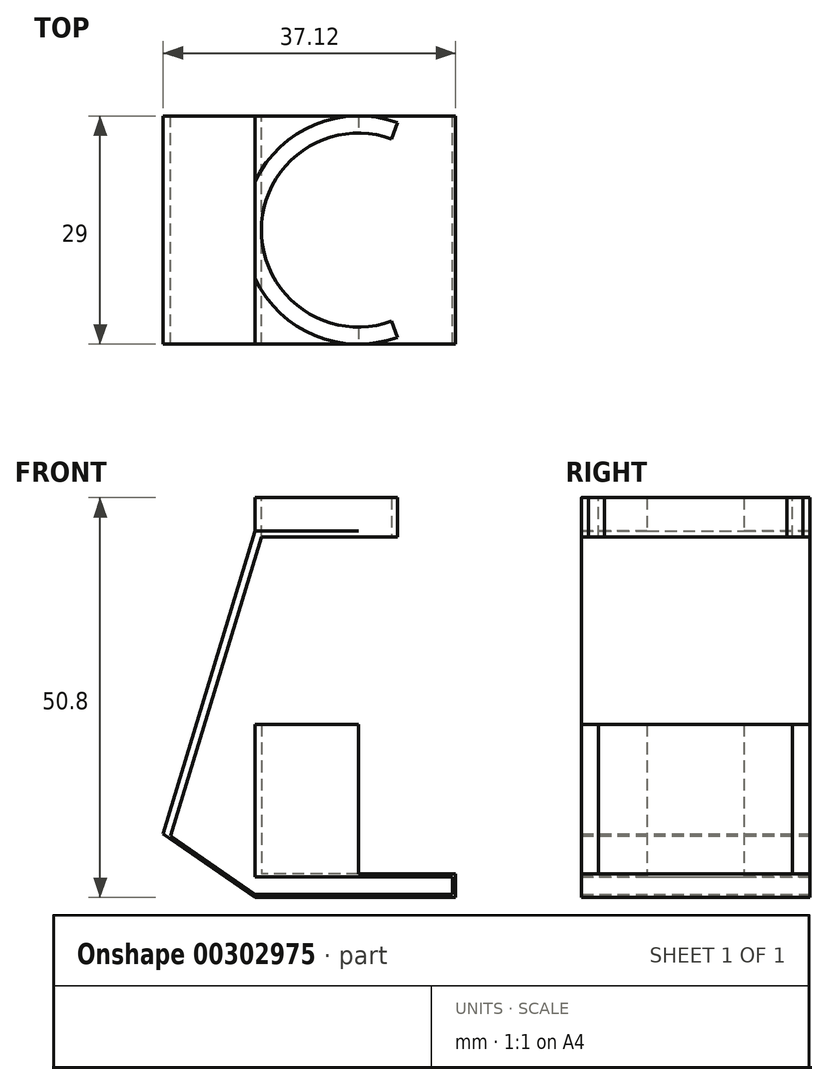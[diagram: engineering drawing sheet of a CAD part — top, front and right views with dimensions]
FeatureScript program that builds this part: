
annotation { "Feature Type Name" : "Feature", "Feature Type Description" : "" }
export const myFeature = defineFeature(function(context is Context, id is Id, definition is map)
    precondition{}
    {
        {
            var Q0;
            Q0=qCreatedBy(makeId("Front.planeOp"),FACE);
            var sketch = newSketch(context, id + "F0", { "sketchPlane" : qUnion([Q0])});
            skLineSegment(sketch, "E0.bottom", {"start": v(12.33, 25.9) * mm, "end": v(-12.32, 25.9) * mm, "construction": true});
            skLineSegment(sketch, "E0.top", {"start": v(12.32, -25.9) * mm, "end": v(-12.33, -25.9) * mm, "construction": true});
            skLineSegment(sketch, "E0.left", {"start": v(12.33, 25.9) * mm, "end": v(12.32, -25.9) * mm, "construction": true});
            skLineSegment(sketch, "E0.right", {"start": v(-12.32, 25.9) * mm, "end": v(-12.33, -25.9) * mm, "construction": true});
            skPoint(sketch, "E0.middle", {"position": v(0, 0) * mm});
            skLineSegment(sketch, "E1", {"start": v(-23.03, -24.9) * mm, "end": v(28, -24.9) * mm, "construction": true});
            skLineSegment(sketch, "E2", {"start": v(-23.03, -21.9) * mm, "end": v(28, -21.9) * mm, "construction": true});
            skLineSegment(sketch, "E3", {"start": v(-19.74, 20.9) * mm, "end": v(18.66, 20.9) * mm, "construction": true});
            skLineSegment(sketch, "E4", {"start": v(-19.74, 21.7) * mm, "end": v(18.66, 21.7) * mm, "construction": true});
            skLineSegment(sketch, "E5", {"start": v(-13.12, 26.29) * mm, "end": v(-13.13, -32.94) * mm, "construction": true});
            skLineSegment(sketch, "E6", {"start": v(-13.13, 21.7) * mm, "end": v(-24.8, -16.79) * mm});
            skLineSegment(sketch, "E7", {"start": v(-24.8, -16.79) * mm, "end": v(-13.13, -24.9) * mm});
            skLineSegment(sketch, "E8", {"start": v(-13.13, -24.9) * mm, "end": v(12.32, -24.9) * mm});
            skLineSegment(sketch, "E9", {"start": v(12.33, -24.9) * mm, "end": v(12.32, -21.9) * mm});
            skLineSegment(sketch, "E10", {"start": v(12.32, -21.9) * mm, "end": v(-13.13, -21.9) * mm});
            skLineSegment(sketch, "E11", {"start": v(-13.13, 21.7) * mm, "end": v(0, 21.7) * mm});
            skLineSegment(sketch, "E12", {"start": v(0, 21.7) * mm, "end": v(0, 20.9) * mm});
            skLineSegment(sketch, "E13", {"start": v(0, 20.9) * mm, "end": v(-12.32, 20.9) * mm});
            skLineSegment(sketch, "E14", {"start": v(-13.13, -24.5) * mm, "end": v(11.93, -24.5) * mm});
            skLineSegment(sketch, "E15", {"start": v(-13.12, -22.3) * mm, "end": v(11.93, -22.3) * mm});
            skLineSegment(sketch, "E16", {"start": v(11.93, -22.3) * mm, "end": v(11.93, -24.5) * mm});
            skLineSegment(sketch, "E17", {"start": v(-13.12, -21.9) * mm, "end": v(-13.12, -22.3) * mm});
            skLineSegment(sketch, "E18", {"start": v(-13.13, -24.5) * mm, "end": v(-23.84, -17.05) * mm});
            skLineSegment(sketch, "E19", {"start": v(-12.32, 20.9) * mm, "end": v(-23.84, -17.05) * mm});
            skSolve(sketch);
        }
        {
            var Q0;
            Q0=makeQuery(id+"F0.imprint","IMPRINT",FACE,{"disambiguationData":[TD([[makeQuery(id+"F0.imprint","IMPRINT",EDGE,{"derivedFrom":sQuery(id+"F0.wireOp",EDGE,"E6")}),1.0]])]});
            extrude(context, id + "F1", {"entities" : qUnion([Q0]), "endBound" : BoundingType.SYMMETRIC, "depth" : 29 * mm, "offsetDistance" : 25 * mm});
        }
        {
            var Q0;
            Q0=makeQuery(id+"F1.opExtrude","SWEPT_FACE",FACE,{"disambiguationData":[OSD([sQuery(id+"F0.wireOp",EDGE,"E11")])]});
            var sketch = newSketch(context, id + "F2", { "sketchPlane" : qUnion([Q0])});
            skCircle(sketch, "E20", {"center": v(0, 0) * mm, "radius": 12.32 * mm});
            skCircle(sketch, "E21", {"center": v(0, 0) * mm, "radius": 14.5 * mm});
            skLineSegment(sketch, "E22", {"start": v(0, 0) * mm, "end": v(4.96, 13.63) * mm});
            skLineSegment(sketch, "E23", {"start": v(0, 0) * mm, "end": v(4.96, -13.63) * mm});
            skSolve(sketch);
        }
        {
            var Q0;
            {var subQ0=sQuery(id+"F2.wireOp",EDGE,"E20");var subQ1=makeQuery(id+"F1.opExtrude","SWEPT_EDGE",EDGE,{"disambiguationData":[OSD([sQuery(id+"F0.wireOp",EDGE,"E11"),sQuery(id+"F0.wireOp",EDGE,"E12")])]});var subQ2=makeQuery(id+"F2.imprint","INTERSECT",VERTEX,{"disambiguationData":[OD(0.0)],"derivedFrom":[subQ1,subQ0]});Q0=makeQuery(id+"F2.imprint","IMPRINT",FACE,{"disambiguationData":[TD([[makeQuery(id+"F2.imprint","IMPRINT",EDGE,{"disambiguationData":[TD([[subQ2,-1.0]])],"derivedFrom":subQ0}),1.0]])]});}
            extrude(context, id + "F3", {"entities" : qUnion([Q0]), "operationType" : NewBodyOperationType.REMOVE, "oppositeDirection" : true, "depth" : 1 * mm, "offsetDistance" : 25 * mm});
        }
        {
            var Q0;
            {var subQ1=sQuery(id+"F0.wireOp",EDGE,"E11");var subQ5=makeQuery(id+"F1.opExtrude","SWEPT_EDGE",EDGE,{"disambiguationData":[OSD([subQ1,sQuery(id+"F0.wireOp",EDGE,"E12")])]});var subQ8=sQuery(id+"F2.wireOp",EDGE,"E20");var subQ9=makeQuery(id+"F2.imprint","INTERSECT",VERTEX,{"disambiguationData":[OD(0.0)],"derivedFrom":[subQ5,subQ8]});Q0=makeQuery(id+"F2.imprint","IMPRINT",FACE,{"disambiguationData":[TD([[makeQuery(id+"F2.imprint","IMPRINT",EDGE,{"disambiguationData":[TD([[subQ9,-1.0]])],"derivedFrom":subQ8}),-1.0]])]});}
            var Q1;
            {var subQ0=sQuery(id+"F2.wireOp",EDGE,"E22");var subQ6=sQuery(id+"F2.wireOp",EDGE,"E21");var subQ8=makeQuery(id+"F2.imprint","INTERSECT",VERTEX,{"derivedFrom":[subQ6,subQ0]});Q1=makeQuery(id+"F2.imprint","IMPRINT",FACE,{"disambiguationData":[TD([[makeQuery(id+"F2.imprint","IMPRINT",EDGE,{"disambiguationData":[TD([[subQ8,1.0]])],"derivedFrom":subQ0}),1.0]])]});}
            var Q2;
            {var subQ0=sQuery(id+"F2.wireOp",EDGE,"E23");var subQ6=sQuery(id+"F2.wireOp",EDGE,"E21");var subQ8=makeQuery(id+"F2.imprint","INTERSECT",VERTEX,{"derivedFrom":[subQ6,subQ0]});Q2=makeQuery(id+"F2.imprint","IMPRINT",FACE,{"disambiguationData":[TD([[makeQuery(id+"F2.imprint","IMPRINT",EDGE,{"disambiguationData":[TD([[subQ8,1.0]])],"derivedFrom":subQ0}),-1.0]])]});}
            extrude(context, id + "F4", {"entities" : qUnion([Q0, Q1, Q2]), "operationType" : NewBodyOperationType.ADD, "depth" : 4.2 * mm, "offsetDistance" : 25 * mm});
        }
        {
            var Q0;
            {var subQ0=sQuery(id+"F2.wireOp",EDGE,"E23");var subQ6=sQuery(id+"F2.wireOp",EDGE,"E21");var subQ8=makeQuery(id+"F2.imprint","INTERSECT",VERTEX,{"derivedFrom":[subQ6,subQ0]});Q0=makeQuery(id+"F2.imprint","IMPRINT",FACE,{"disambiguationData":[TD([[makeQuery(id+"F2.imprint","IMPRINT",EDGE,{"disambiguationData":[TD([[subQ8,1.0]])],"derivedFrom":subQ0}),-1.0]])]});}
            var Q1;
            {var subQ0=sQuery(id+"F2.wireOp",EDGE,"E22");var subQ6=sQuery(id+"F2.wireOp",EDGE,"E21");var subQ8=makeQuery(id+"F2.imprint","INTERSECT",VERTEX,{"derivedFrom":[subQ6,subQ0]});Q1=makeQuery(id+"F2.imprint","IMPRINT",FACE,{"disambiguationData":[TD([[makeQuery(id+"F2.imprint","IMPRINT",EDGE,{"disambiguationData":[TD([[subQ8,1.0]])],"derivedFrom":subQ0}),1.0]])]});}
            extrude(context, id + "F5", {"entities" : qUnion([Q0, Q1]), "operationType" : NewBodyOperationType.ADD, "oppositeDirection" : true, "depth" : 0.8 * mm, "offsetDistance" : 25 * mm});
        }
        {
            var Q0;
            Q0=makeQuery(id+"F1.opExtrude","SWEPT_FACE",FACE,{"disambiguationData":[OSD([sQuery(id+"F0.wireOp",EDGE,"E10")])]});
            var sketch = newSketch(context, id + "F6", { "sketchPlane" : qUnion([Q0])});
            skCircle(sketch, "E24", {"center": v(0, 0) * mm, "radius": 12.32 * mm});
            skCircle(sketch, "E25", {"center": v(0, 0) * mm, "radius": 14.5 * mm});
            skLineSegment(sketch, "E26", {"start": v(0, 14.5) * mm, "end": v(0, -14.5) * mm});
            skSolve(sketch);
        }
        {
            var Q0;
            {var subQ0=sQuery(id+"F6.wireOp",EDGE,"E26");var subQ1=sQuery(id+"F6.wireOp",EDGE,"E24");var subQ2=makeQuery(id+"F6.imprint","INTERSECT",VERTEX,{"disambiguationData":[OD(0.0)],"derivedFrom":[subQ1,subQ0]});Q0=makeQuery(id+"F6.imprint","IMPRINT",FACE,{"disambiguationData":[TD([[makeQuery(id+"F6.imprint","IMPRINT",EDGE,{"disambiguationData":[TD([[subQ2,-1.0]])],"derivedFrom":subQ1}),-1.0]])]});}
            extrude(context, id + "F7", {"entities" : qUnion([Q0]), "operationType" : NewBodyOperationType.ADD, "depth" : 19 * mm, "offsetDistance" : 25 * mm});
        }
        {
            var Q0;
            {var subQ0=sQuery(id+"F6.wireOp",EDGE,"E25");var subQ1=sQuery(id+"F0.wireOp",EDGE,"E10");var subQ2=makeQuery(id+"F1.opExtrude","CAP_EDGE",EDGE,{"disambiguationData":[OSD([subQ1])],"isStart":true});var subQ3=makeQuery(id+"F6.imprint","INTERSECT",VERTEX,{"derivedFrom":[subQ2,subQ0,sQuery(id+"F6.wireOp",EDGE,"E26")]});Q0=makeQuery(id+"F6.imprint","IMPRINT",FACE,{"disambiguationData":[TD([[makeQuery(id+"F6.imprint","IMPRINT",EDGE,{"disambiguationData":[TD([[subQ3,-1.0]])],"derivedFrom":subQ0}),-1.0]])]});}
            var Q1;
            {var subQ0=sQuery(id+"F6.wireOp",EDGE,"E25");var subQ1=sQuery(id+"F0.wireOp",EDGE,"E10");var subQ2=makeQuery(id+"F1.opExtrude","CAP_EDGE",EDGE,{"disambiguationData":[OSD([subQ1])],"isStart":false});var subQ3=makeQuery(id+"F6.imprint","INTERSECT",VERTEX,{"derivedFrom":[subQ2,subQ0,sQuery(id+"F6.wireOp",EDGE,"E26")]});Q1=makeQuery(id+"F6.imprint","IMPRINT",FACE,{"disambiguationData":[TD([[makeQuery(id+"F6.imprint","IMPRINT",EDGE,{"disambiguationData":[TD([[subQ3,1.0]])],"derivedFrom":subQ0}),-1.0]])]});}
            extrude(context, id + "F8", {"entities" : qUnion([Q0, Q1]), "operationType" : NewBodyOperationType.REMOVE, "oppositeDirection" : true, "depth" : 1 * mm, "offsetDistance" : 25 * mm});
        }
    });
